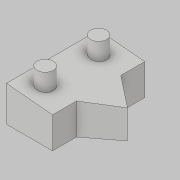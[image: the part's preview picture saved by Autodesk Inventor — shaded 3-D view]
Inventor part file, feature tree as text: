
AUTODESK INVENTOR PART (.ipt)
format: ipt  version: 2019 (Build 230136000, 136)  size: 126,464 bytes
history: native  units: mm
features: extrude x3, sketch x3, shell x1
ambient origin geometry x8: Origin, YZ Plane, XZ Plane, XY Plane, X Axis, Y Axis, Z Axis, Center Point
bodies: Solid1 (feature_tree)
feature tree (7):
  extrude  "Extrusion1"  Depth=200.0mm
  extrude  "Extrusion2"  Depth=42.0mm
  extrude  "Extrusion3"  TaperAngle=75.0deg  [1 undecoded]
  shell  "Shell1"  Thickness=52.0mm
  sketch  "Sketch1"  dims[d0=100.0mm d1=200.0mm]
  sketch  "Sketch2"  dims[d2=35.0mm d4=42.0mm]
  sketch  "Sketch3"  dims[d5=42.0mm d6=75.0deg d7=52.0mm d8=110.0mm d9=0.0mm d11=62.0mm d12=77.0mm d13=110.0mm d14=0.0mm d22=110.0mm d23=0.0mm d24=4.0mm]
note: 1 required parameter value undecoded (feature->parameter linkage not recoverable at this tier; creation-order binding heuristic only, values carry confidence <= 0.55)
